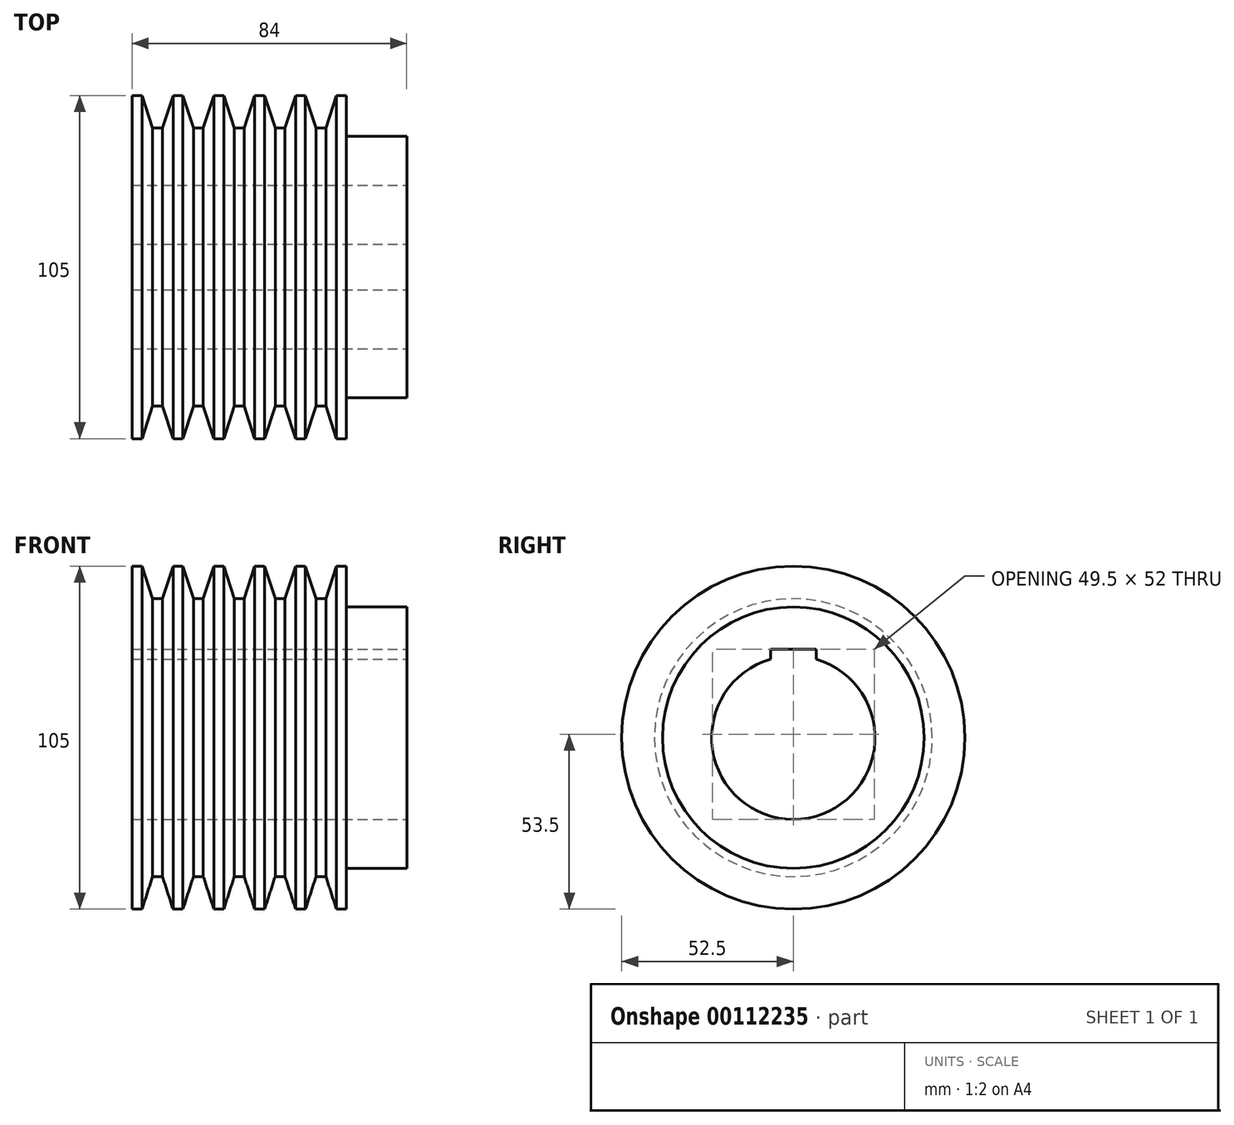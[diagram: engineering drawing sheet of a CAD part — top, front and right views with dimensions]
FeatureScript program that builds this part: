
annotation { "Feature Type Name" : "Feature", "Feature Type Description" : "" }
export const myFeature = defineFeature(function(context is Context, id is Id, definition is map)
    precondition{}
    {
        {
            var Q0;
            Q0=qCreatedBy(makeId("Front.planeOp"),FACE);
            var sketch = newSketch(context, id + "F0", { "sketchPlane" : qUnion([Q0])});
            skLineSegment(sketch, "E0", {"start": v(38.54, 0) * mm, "end": v(38.54, 52.5) * mm});
            skLineSegment(sketch, "E1", {"start": v(104.04, 52.5) * mm, "end": v(104.04, 40) * mm});
            skLineSegment(sketch, "E2", {"start": v(104.04, 40) * mm, "end": v(122.54, 40) * mm});
            skLineSegment(sketch, "E3", {"start": v(122.54, 40) * mm, "end": v(122.54, 0) * mm});
            skLineSegment(sketch, "E4", {"start": v(38.54, 52.5) * mm, "end": v(41.54, 52.5) * mm});
            skLineSegment(sketch, "E5", {"start": v(41.54, 52.5) * mm, "end": v(44.8, 42.5) * mm});
            skLineSegment(sketch, "E6", {"start": v(44.8, 42.5) * mm, "end": v(47.8, 42.5) * mm});
            skLineSegment(sketch, "E7", {"start": v(47.8, 42.5) * mm, "end": v(51.04, 52.5) * mm});
            skLineSegment(sketch, "E8", {"start": v(51.04, 52.5) * mm, "end": v(54.04, 52.5) * mm});
            skLineSegment(sketch, "E9", {"start": v(54.04, 52.5) * mm, "end": v(57.3, 42.5) * mm});
            skLineSegment(sketch, "E10", {"start": v(57.3, 42.5) * mm, "end": v(60.3, 42.5) * mm});
            skLineSegment(sketch, "E11", {"start": v(60.3, 42.5) * mm, "end": v(63.54, 52.5) * mm});
            skLineSegment(sketch, "E12", {"start": v(63.54, 52.5) * mm, "end": v(66.54, 52.5) * mm});
            skLineSegment(sketch, "E13", {"start": v(66.54, 52.5) * mm, "end": v(69.8, 42.5) * mm});
            skLineSegment(sketch, "E14", {"start": v(69.8, 42.5) * mm, "end": v(72.8, 42.5) * mm});
            skLineSegment(sketch, "E15", {"start": v(72.8, 42.5) * mm, "end": v(76.04, 52.5) * mm});
            skLineSegment(sketch, "E16", {"start": v(76.04, 52.5) * mm, "end": v(79.04, 52.5) * mm});
            skLineSegment(sketch, "E17", {"start": v(91.54, 52.5) * mm, "end": v(94.8, 42.5) * mm});
            skLineSegment(sketch, "E18", {"start": v(94.8, 42.5) * mm, "end": v(97.8, 42.5) * mm});
            skLineSegment(sketch, "E19", {"start": v(97.8, 42.5) * mm, "end": v(101.04, 52.5) * mm});
            skLineSegment(sketch, "E20", {"start": v(101.04, 52.5) * mm, "end": v(104.04, 52.5) * mm});
            skLineSegment(sketch, "E21", {"start": v(79.04, 52.5) * mm, "end": v(82.3, 42.5) * mm});
            skLineSegment(sketch, "E22", {"start": v(82.3, 42.5) * mm, "end": v(85.3, 42.5) * mm});
            skLineSegment(sketch, "E23", {"start": v(85.3, 42.5) * mm, "end": v(88.54, 52.5) * mm});
            skLineSegment(sketch, "E24", {"start": v(88.54, 52.5) * mm, "end": v(91.54, 52.5) * mm});
            skLineSegment(sketch, "E25", {"start": v(122.54, 0) * mm, "end": v(38.54, 0) * mm});
            skSolve(sketch);
        }
        {
            var Q0;
            Q0=makeQuery(id+"F0.imprint","IMPRINT",FACE,{"disambiguationData":[TD([[makeQuery(id+"F0.imprint","IMPRINT",EDGE,{"derivedFrom":sQuery(id+"F0.wireOp",EDGE,"E0")}),-1.0]])]});
            var Q1;
            Q1=sQuery(id+"F0.wireOp",EDGE,"E25");
            revolve(context, id + "F1", {"entities" : qUnion([Q0]), "axis" : qUnion([Q1]), "revolveType" : RevolveType.FULL});
        }
        {
            var Q0;
            Q0=makeQuery(id+"F1.opRevolve","SWEPT_FACE",FACE,{"disambiguationData":[OSD([sQuery(id+"F0.wireOp",EDGE,"E3")])]});
            var sketch = newSketch(context, id + "F2", { "sketchPlane" : qUnion([Q0])});
            skCircle(sketch, "E26", {"center": v(0, 0) * mm, "radius": 25 * mm});
            skSolve(sketch);
        }
        {
            var Q0;
            Q0=makeQuery(id+"F2.imprint","IMPRINT",FACE,{"disambiguationData":[TD([[makeQuery(id+"F2.imprint","IMPRINT",EDGE,{"derivedFrom":sQuery(id+"F2.wireOp",EDGE,"E26")}),1.0]])]});
            extrude(context, id + "F3", {"entities" : qUnion([Q0]), "operationType" : NewBodyOperationType.REMOVE, "oppositeDirection" : true, "depth" : 84 * mm});
        }
        {
            var Q0;
            Q0=makeQuery(id+"F1.opRevolve","SWEPT_FACE",FACE,{"disambiguationData":[OSD([sQuery(id+"F0.wireOp",EDGE,"E3")])]});
            var sketch = newSketch(context, id + "F4", { "sketchPlane" : qUnion([Q0])});
            skLineSegment(sketch, "E27", {"start": v(-7, 24) * mm, "end": v(-7, 27) * mm});
            skLineSegment(sketch, "E28", {"start": v(-7, 27) * mm, "end": v(7, 27) * mm});
            skLineSegment(sketch, "E29", {"start": v(7, 27) * mm, "end": v(7, 24) * mm});
            skSolve(sketch);
        }
        {
            var Q0;
            {var subQ0=sQuery(id+"F4.wireOp",EDGE,"E27");Q0=makeQuery(id+"F4.imprint","IMPRINT",FACE,{"disambiguationData":[TD([[makeQuery(id+"F4.imprint","IMPRINT",EDGE,{"derivedFrom":subQ0}),-1.0]])]});}
            extrude(context, id + "F5", {"entities" : qUnion([Q0]), "operationType" : NewBodyOperationType.REMOVE, "oppositeDirection" : true, "depth" : 84 * mm});
        }
    });
